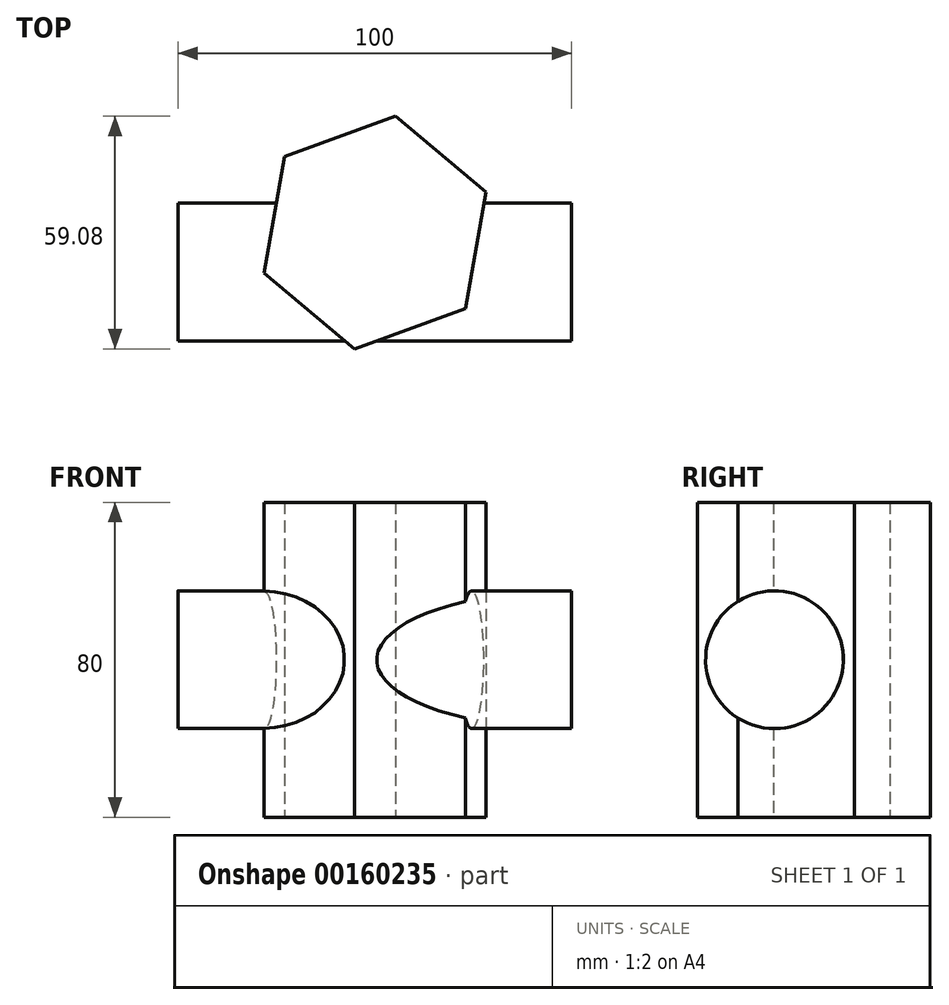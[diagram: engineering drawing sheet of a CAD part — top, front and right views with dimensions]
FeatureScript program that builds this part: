
annotation { "Feature Type Name" : "Feature", "Feature Type Description" : "" }
export const myFeature = defineFeature(function(context is Context, id is Id, definition is map)
    precondition{}
    {
        {
            var Q0;
            Q0=qCreatedBy(makeId("Top.planeOp"),FACE);
            var sketch = newSketch(context, id + "F0", { "sketchPlane" : qUnion([Q0])});
            skCircle(sketch, "E0.cCircle", {"center": v(0, 0) * mm, "radius": 25.98 * mm, "construction": true});
            skLineSegment(sketch, "E0.0", {"start": v(5.2, 29.54) * mm, "end": v(28.2, 10.26) * mm});
            skLineSegment(sketch, "E0.1", {"start": v(28.2, 10.26) * mm, "end": v(22.98, -19.28) * mm});
            skLineSegment(sketch, "E0.2", {"start": v(22.98, -19.28) * mm, "end": v(-5.2, -29.54) * mm});
            skLineSegment(sketch, "E0.3", {"start": v(-5.2, -29.54) * mm, "end": v(-28.2, -10.26) * mm});
            skLineSegment(sketch, "E0.4", {"start": v(-28.2, -10.26) * mm, "end": v(-22.98, 19.28) * mm});
            skLineSegment(sketch, "E0.5", {"start": v(-22.98, 19.28) * mm, "end": v(5.2, 29.54) * mm});
            skPoint(sketch, "E0.0.midPoint", {"position": v(16.7, 19.9) * mm});
            skLineSegment(sketch, "E1", {"start": v(0, 0) * mm, "end": v(28.2, 10.26) * mm, "construction": true});
            skLineSegment(sketch, "E2", {"start": v(0, 0) * mm, "end": v(28.2, 0) * mm, "construction": true});
            skSolve(sketch);
        }
        {
            var Q0;
            Q0=makeQuery(id+"F0.imprint","IMPRINT",FACE,{"disambiguationData":[TD([[makeQuery(id+"F0.imprint","IMPRINT",EDGE,{"derivedFrom":sQuery(id+"F0.wireOp",EDGE,"E0.0")}),-1.0]])]});
            extrude(context, id + "F1", {"entities" : qUnion([Q0]), "depth" : 80 * mm, "symmetric" : true});
        }
        {
            var Q0;
            Q0=qCreatedBy(makeId("Right.planeOp"),FACE);
            var sketch = newSketch(context, id + "F2", { "sketchPlane" : qUnion([Q0])});
            skCircle(sketch, "E3", {"center": v(-10, 0) * mm, "radius": 17.5 * mm});
            skSolve(sketch);
        }
        {
            var Q0;
            Q0 = qSketchRegion(id + "F2", true);
            extrude(context, id + "F3", {"entities" : qUnion([Q0]), "operationType" : NewBodyOperationType.ADD, "depth" : 100 * mm, "symmetric" : true});
        }
    });
